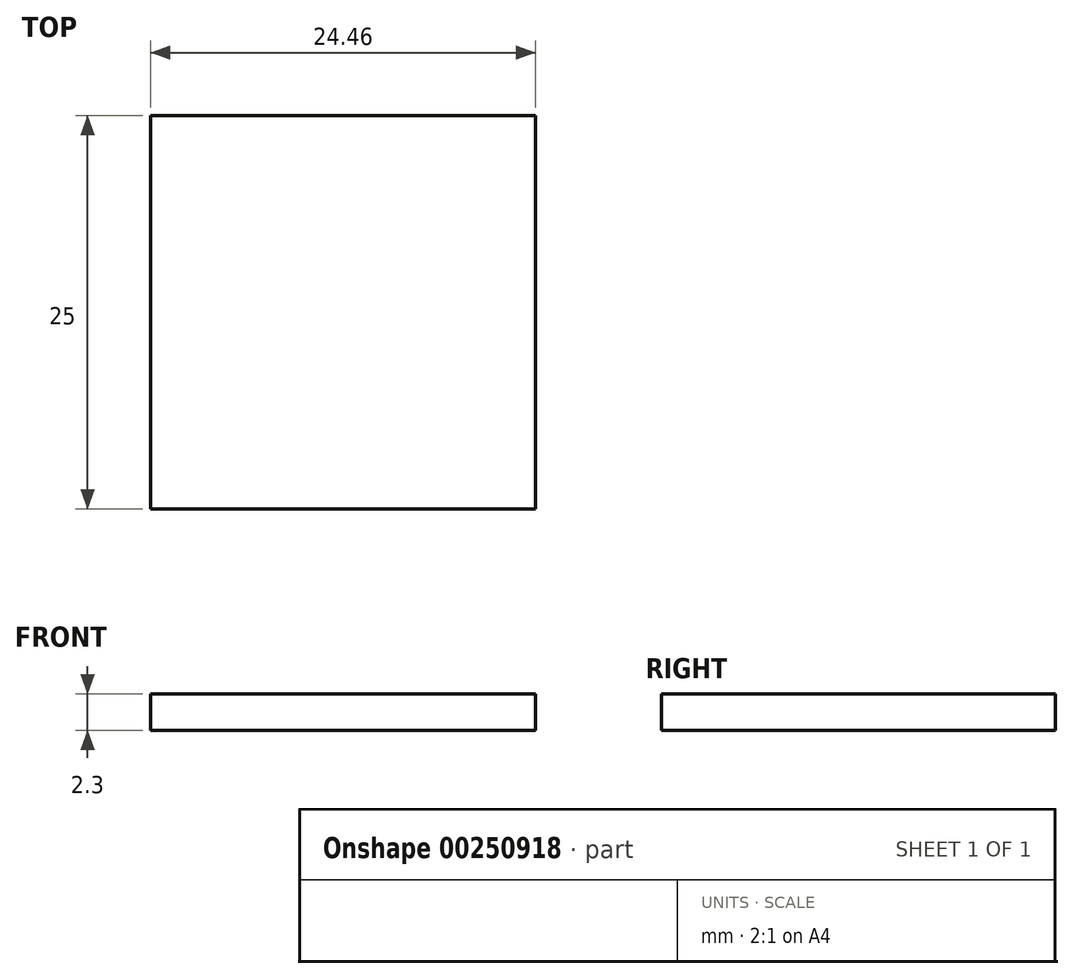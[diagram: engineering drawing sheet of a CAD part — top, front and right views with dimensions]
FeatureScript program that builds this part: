
annotation { "Feature Type Name" : "Feature", "Feature Type Description" : "" }
export const myFeature = defineFeature(function(context is Context, id is Id, definition is map)
    precondition{}
    {
        {
            var Q0;
            Q0=qCreatedBy(makeId("Front.planeOp"),FACE);
            var sketch = newSketch(context, id + "F0", { "sketchPlane" : qUnion([Q0])});
            skLineSegment(sketch, "E0.bottom", {"start": v(-12.23, 1.15) * mm, "end": v(12.23, 1.15) * mm});
            skLineSegment(sketch, "E0.top", {"start": v(-12.23, -1.15) * mm, "end": v(12.23, -1.15) * mm});
            skLineSegment(sketch, "E0.left", {"start": v(-12.23, 1.15) * mm, "end": v(-12.23, -1.15) * mm});
            skLineSegment(sketch, "E0.right", {"start": v(12.23, 1.15) * mm, "end": v(12.23, -1.15) * mm});
            skPoint(sketch, "E0.middle", {"position": v(0, 0) * mm});
            skSolve(sketch);
        }
        {
            var Q0;
            Q0=makeQuery(id+"F0.imprint","IMPRINT",FACE,{"disambiguationData":[TD([[makeQuery(id+"F0.imprint","IMPRINT",EDGE,{"derivedFrom":sQuery(id+"F0.wireOp",EDGE,"E0.bottom")}),-1.0]])]});
            extrude(context, id + "F1", {"entities" : qUnion([Q0]), "depth" : 25 * mm});
        }
    });
